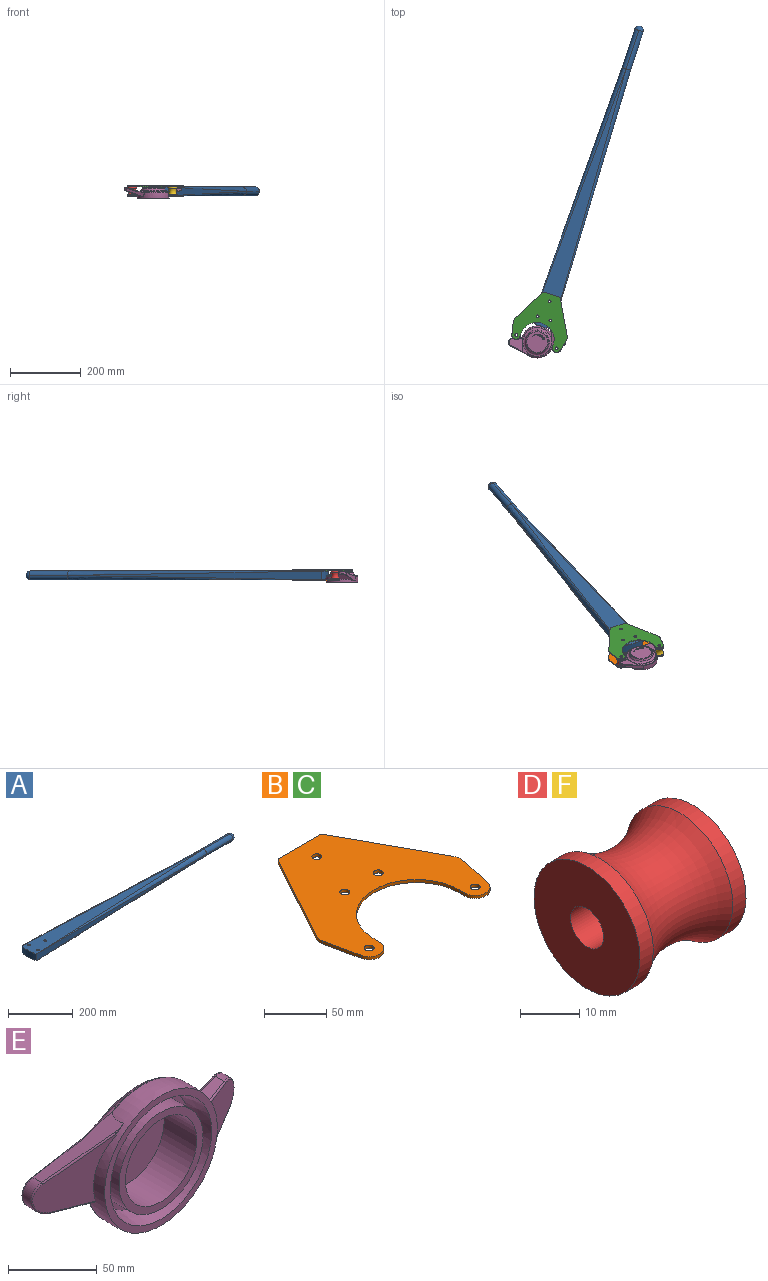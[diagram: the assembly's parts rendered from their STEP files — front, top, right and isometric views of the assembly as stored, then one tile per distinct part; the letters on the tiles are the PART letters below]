
ASSEMBLY  parts=6 mates=8
PART A: 25 faces, bbox 934.5x68.1x25.4 mm
  f0: plane 767.57x64.78mm, normal (0,0,1), area 23938.9mm2, adj f5,f8,f16,f22,f23,f24
  f1: cylinder r=101.76mm len=62.96mm, axis (0,0,-1), area 1577.1mm2, adj f6,f8,f13,f17
  f2: plane 763.77x24.64mm, normal (0.02,1,0), area 9383mm2, adj f5,f6,f11
  f3: sphere r=12.7mm, area 1013.4mm2, adj f4,f10,f15,f19
  f4: cylinder r=12.7mm len=114.46mm, axis (-1,0,0), area 2281.8mm2, adj f3,f5,f10,f15
  f5: bspline ~921.03x35.72mm, area 7832.2mm2, adj f0,f2,f4,f7
  f6: cylinder r=0.38mm len=24.64mm, axis (0,0,-1), area 12mm2, adj f1,f2,f7,f12
  f7: bspline ~0.38x0.38mm, area 0.1mm2, adj f5,f6,f8
  f8: torus R=101.38mm, axis (0,0,-1), area 38.3mm2, adj f0,f1,f7,f18
  f9: plane 767.57x64.78mm, normal (0,0,-1), area 23938.9mm2, adj f11,f13,f20,f22,f23,f24
  f10: cylinder r=12.7mm len=114.46mm, axis (-1,0,0), area 2281.8mm2, adj f3,f4,f11,f19
  f11: bspline ~921.03x35.72mm, area 7832.2mm2, adj f2,f9,f10,f12
  f12: bspline ~0.38x0.38mm, area 0.1mm2, adj f6,f11,f13
  f13: torus R=101.38mm, axis (0,0,1), area 38.3mm2, adj f1,f9,f12,f21
  f14: plane 763.77x24.64mm, normal (0.02,-1,0), area 9383mm2, adj f16,f17,f20
  f15: cylinder r=12.7mm len=114.46mm, axis (-1,0,0), area 2281.8mm2, adj f3,f4,f16,f19
  f16: bspline ~921.03x35.72mm, area 7832.2mm2, adj f0,f14,f15,f18
  f17: cylinder r=0.38mm len=24.64mm, axis (0,0,-1), area 12mm2, adj f1,f14,f18,f21
  f18: bspline ~0.38x0.38mm, area 0.1mm2, adj f8,f16,f17
  f19: cylinder r=12.7mm len=114.46mm, axis (-1,0,0), area 2281.8mm2, adj f3,f10,f15,f20
  f20: bspline ~921.03x35.72mm, area 7832.2mm2, adj f9,f14,f19,f21
  f21: bspline ~0.38x0.38mm, area 0.1mm2, adj f13,f17,f20
  f22: cylinder r=3.98mm len=25.4mm, axis (0,0,1), area 634.4mm2, adj f0,f9
  f23: cylinder r=3.98mm len=25.4mm, axis (0,0,1), area 634.4mm2, adj f0,f9
  f24: cylinder r=3.98mm len=25.4mm, axis (0,0,1), area 634.4mm2, adj f0,f9
PART B: 21 faces, bbox 159.6x151.6x3 mm
  f0: cylinder r=11.94mm len=23.62mm, axis (0,0,1), area 105.1mm2, adj f1,f13,f14,f15
  f1: plane 35.96x7.52mm, normal (-0.98,-0.2,0), area 110.2mm2, adj f0,f2,f14,f15
  f2: cylinder r=12.7mm len=8.69mm, axis (0,0,1), area 26.9mm2, adj f1,f3,f14,f15
  f3: plane 95.84x52.41mm, normal (-0.88,0.48,0), area 327.7mm2, adj f2,f4,f14,f15
  f4: cylinder r=3.17mm len=3mm, axis (0,0,1), area 10.2mm2, adj f3,f5,f14,f15
  f5: plane 46.09x3mm, normal (0,1,0), area 138.3mm2, adj f4,f6,f14,f15
  f6: cylinder r=3.17mm len=3mm, axis (0,0,1), area 10.2mm2, adj f5,f7,f14,f15
  f7: plane 95.84x52.41mm, normal (0.88,0.48,0), area 327.7mm2, adj f6,f8,f14,f15
  f8: cylinder r=12.7mm len=8.69mm, axis (0,0,1), area 26.9mm2, adj f7,f9,f14,f15
  f9: plane 35.96x7.52mm, normal (0.98,-0.2,0), area 110.2mm2, adj f8,f10,f14,f15
  f10: cylinder r=11.94mm len=23.62mm, axis (0,0,1), area 105.1mm2, adj f9,f11,f14,f15
  f11: plane 6.35x3mm, normal (-1,0,0), area 19mm2, adj f10,f12,f14,f15
  f12: cylinder r=48.39mm len=96.77mm, axis (0,0,1), area 456mm2, adj f11,f13,f14,f15
  f13: plane 6.35x3mm, normal (1,0,0), area 19mm2, adj f0,f12,f14,f15
  f14: plane 159.6x151.64mm, normal (0,0,-1), area 12441.6mm2, adj f0,f1,f2,f3,f4,f5,f6,f7
  f15: plane 159.6x151.64mm, normal (0,0,1), area 12441.6mm2, adj f0,f1,f2,f3,f4,f5,f6,f7
  f16: cylinder r=3.98mm len=7.95mm, axis (0,0,1), area 74.9mm2, adj f14,f15
  f17: cylinder r=3.98mm len=7.95mm, axis (0,0,1), area 74.9mm2, adj f14,f15
  f18: cylinder r=3.98mm len=7.95mm, axis (0,0,1), area 74.9mm2, adj f14,f15
  f19: cylinder r=3.98mm len=7.95mm, axis (0,0,1), area 74.9mm2, adj f14,f15
  f20: cylinder r=3.98mm len=7.95mm, axis (0,0,1), area 74.9mm2, adj f14,f15
PART C: same geometry as B
PART D: 6 faces, bbox 25.4x30.6x30.6 mm
  f0: plane 25.4x25.4mm, normal (1,0,0), area 457.1mm2, adj f1,f5
  f1: cylinder r=12.7mm len=25.4mm, axis (-1,0,0), area 253.4mm2, adj f0,f2
  f2: torus R=25.4mm, axis (-1,0,0), area 1360.5mm2, adj f1,f3
  f3: cylinder r=12.7mm len=25.4mm, axis (-1,0,0), area 253.4mm2, adj f2,f4
  f4: plane 25.4x25.4mm, normal (-1,0,0), area 457.1mm2, adj f3,f5
  f5: cylinder r=3.98mm len=25.4mm, axis (-1,0,0), area 634.4mm2, adj f0,f4
PART E: 111 faces, bbox 162.9x31.9x99.3 mm
  f0: plane 58.91x58.91mm, normal (0,1,0), area 2670.1mm2, adj f26,f55,f56,f57,f58,f64,f65,f66
  f1: plane 81.99x81.73mm, normal (0,1,0), area 374.9mm2, adj f2,f5,f11,f23,f24,f27,f30,f35
  f2: cylinder r=7mm len=38.39mm, axis (0,0,1), area 77.7mm2, adj f1,f3,f43,f47
  f3: plane 37.36x37.18mm, normal (0.29,0.96,0), area 1035.3mm2, adj f2,f44,f45,f46
  f4: plane 27.66x17.22mm, normal (0,0,-1), area 218mm2, adj f7,f10,f18,f25,f46,f47,f54
  f5: plane 5.19x4.14mm, normal (1,0,0), area 1.4mm2, adj f1,f17,f24,f42
  f6: plane 51.49x27.07mm, normal (-0.46,0,0.89), area 518.6mm2, adj f7,f8,f12,f18,f42,f43,f44,f52
  f7: cylinder r=12mm len=22.64mm, axis (0,-1,0), area 231.1mm2, adj f4,f6,f45,f53
  f8: plane 7.51x6.59mm, normal (0,-1,0), area 5.7mm2, adj f6,f9,f18,f52
  f9: plane 47.7x42.59mm, normal (-0.36,-0.93,0), area 1080.8mm2, adj f8,f18,f52,f53,f54
  f10: torus R=38.12mm, axis (0,1,0), area 327.7mm2, adj f4,f11,f25,f30,f35,f47
  f11: torus R=40.82mm, axis (0,1,0), area 113.7mm2, adj f1,f10,f30,f47,f48
  f12: torus R=42.54mm, axis (0,-1,0), area 70.5mm2, adj f6,f17,f18,f29,f42
  f13: plane 67.1x67.1mm, normal (0,-1,0), area 984.7mm2, adj f14,f22
  f14: cylinder r=28.5mm len=57mm, axis (0,1,0), area 4655.8mm2, adj f13,f15
  f15: plane 57x57mm, normal (0,-1,0), area 2551.8mm2, adj f14
  f16: cone r=31mm half-angle=26.6deg, axis (0,-1,0), area 1096.7mm2, adj f23,f26
  f17: torus R=38.12mm, axis (0,1,0), area 327.9mm2, adj f5,f12,f24,f29,f40,f42
  f18: revolved ~90.6x90.6mm, area 3305.4mm2, adj f4,f6,f8,f9,f12,f19,f25,f29
  f19: plane 90x90mm, normal (0,-1,0), area 1208.7mm2, adj f18,f20
  f20: cone r=40.5mm half-angle=11.3deg, axis (0,-1,0), area 3748.5mm2, adj f19,f21
  f21: plane 75x75mm, normal (0,-1,0), area 881.4mm2, adj f20,f22
  f22: cylinder r=33.55mm len=67.1mm, axis (0,1,0), area 3162.1mm2, adj f13,f21
  f23: torus R=40.33mm, axis (0,1,0), area 1793.5mm2, adj f1,f16
  f24: torus R=40.82mm, axis (0,1,0), area 114.3mm2, adj f1,f5,f17,f40,f41
  f25: torus R=42.54mm, axis (0,-1,0), area 70.5mm2, adj f4,f10,f18,f31,f35
  f26: torus R=29.45mm, axis (0,1,0), area 534mm2, adj f0,f16
  f27: cylinder r=7mm len=37.32mm, axis (0,0,-1), area 71.4mm2, adj f1,f28,f36,f40
  f28: plane 36.71x36.04mm, normal (-0.29,0.96,0), area 982.7mm2, adj f27,f37,f38,f39
  f29: plane 27.15x16.67mm, normal (0,0,1), area 203.7mm2, adj f12,f17,f18,f32,f39,f40,f51
  f30: plane 5.2x4.14mm, normal (-1,0,0), area 1.4mm2, adj f1,f10,f11,f35
  f31: plane 51.36x26.98mm, normal (0.46,0,-0.89), area 490.3mm2, adj f18,f25,f32,f33,f35,f36,f37,f49
  f32: cylinder r=12mm len=22.64mm, axis (0,-1,0), area 213.3mm2, adj f29,f31,f38,f50
  f33: plane 7.51x6.59mm, normal (0,-1,0), area 5.7mm2, adj f18,f31,f34,f49
  f34: plane 47.7x42.59mm, normal (0.36,-0.93,0), area 1080.8mm2, adj f18,f33,f49,f50,f51
  f35: bspline ~27.86x14.91mm, area 92.6mm2, adj f1,f10,f25,f30,f31,f36
  f36: bspline ~3.16x2.62mm, area 6.3mm2, adj f27,f31,f35,f37
  f37: cylinder r=1.5mm len=32.2mm, axis (-0.86,-0.26,-0.45), area 92.8mm2, adj f28,f31,f36,f38
  f38: bspline ~23.46x14.49mm, area 83.2mm2, adj f28,f32,f37,f39
  f39: cylinder r=1.5mm len=26.65mm, axis (0.96,0.29,0), area 64.5mm2, adj f28,f29,f38,f40
  f40: torus R=8.5mm, axis (0,0,1), area 3.8mm2, adj f17,f24,f27,f29,f39,f41
  f41: cylinder r=1.5mm len=0.63mm, axis (1,0,0), area 0.2mm2, adj f1,f24,f40
  f42: bspline ~27.58x14.32mm, area 82.6mm2, adj f1,f5,f6,f12,f17,f43
  f43: bspline ~2.78x2.1mm, area 4.1mm2, adj f2,f6,f42,f44
  f44: cylinder r=1mm len=32.2mm, axis (0.86,-0.26,0.45), area 62.6mm2, adj f3,f6,f43,f45
  f45: bspline ~23.4x14.35mm, area 56.2mm2, adj f3,f7,f44,f46
  f46: cylinder r=1mm len=26.65mm, axis (-0.96,0.29,0), area 43.3mm2, adj f3,f4,f45,f47
  f47: torus R=8mm, axis (0,0,-1), area 2.8mm2, adj f2,f4,f10,f11,f46,f48
  f48: cylinder r=1mm len=0.75mm, axis (-1,0,0), area 0.2mm2, adj f1,f11,f47
  f49: cylinder r=1mm len=44.4mm, axis (0.84,0.32,0.44), area 72mm2, adj f31,f33,f34,f50
  f50: bspline ~22.64x12mm, area 41.6mm2, adj f32,f34,f49,f51
  f51: cylinder r=1mm len=25.54mm, axis (-0.93,-0.36,0), area 42.3mm2, adj f18,f29,f34,f50
  f52: cylinder r=1mm len=44.4mm, axis (-0.84,0.32,-0.44), area 72mm2, adj f6,f8,f9,f53
  f53: bspline ~22.64x12mm, area 41.6mm2, adj f7,f9,f52,f54
  f54: cylinder r=1mm len=25.54mm, axis (0.93,-0.36,0), area 42.3mm2, adj f4,f9,f18,f53
  f55: extruded ~3.24x1.19mm, area 0.4mm2, adj f0,f56,f58,f59
  f56: extruded ~3.32x1.28mm, area 0.4mm2, adj f0,f55,f57,f59
  f57: extruded ~3.27x1.25mm, area 0.4mm2, adj f0,f56,f58,f59
  f58: extruded ~3.25x1.28mm, area 0.4mm2, adj f0,f55,f57,f59
  f59: plane 4.9x4.86mm, normal (0,1,0), area 8.1mm2, adj f55,f56,f57,f58,f60,f61,f62,f63
  f60: extruded ~2.53x0.92mm, area 0.3mm2, adj f59,f61,f63,f109
  f61: extruded ~2.41x1.02mm, area 0.3mm2, adj f59,f60,f62,f109
  f62: extruded ~2.47x0.9mm, area 0.3mm2, adj f59,f61,f63,f109
  f63: extruded ~2.38x0.96mm, area 0.3mm2, adj f59,f60,f62,f109
  f64: plane 0.56x0.3mm, normal (0.47,0,-0.89), area 0.1mm2, adj f0,f65,f73,f74
  f65: plane 4.1x2.15mm, normal (0.89,0,0.46), area 0.5mm2, adj f0,f64,f66,f74
  f66: plane 0.6x0.32mm, normal (-0.47,0,0.89), area 0.1mm2, adj f0,f65,f67,f74
  f67: plane 4.44x0.64mm, normal (-0.99,0,0.14), area 0.4mm2, adj f0,f66,f68,f74
  f68: plane 3.22x1.69mm, normal (0.89,0,0.46), area 0.4mm2, adj f0,f67,f69,f74
  f69: plane 0.56x0.3mm, normal (-0.47,0,0.89), area 0.1mm2, adj f0,f68,f70,f74
  f70: plane 4.1x2.15mm, normal (-0.89,0,-0.46), area 0.5mm2, adj f0,f69,f71,f74
  f71: plane 0.6x0.32mm, normal (0.47,0,-0.89), area 0.1mm2, adj f0,f70,f72,f74
  f72: plane 4.44x0.64mm, normal (0.99,0,-0.14), area 0.4mm2, adj f0,f71,f73,f74
  f73: plane 3.22x1.69mm, normal (-0.89,0,-0.46), area 0.4mm2, adj f0,f64,f72,f74
  f74: plane 5.93x5.65mm, normal (0,1,0), area 8.7mm2, adj f64,f65,f66,f67,f68,f69,f70,f71
  f75: plane 1.31x1.25mm, normal (0.69,0,-0.72), area 0.2mm2, adj f0,f76,f81,f82
  f76: plane 3.33x3.19mm, normal (0.72,0,0.69), area 0.5mm2, adj f0,f75,f77,f82
  f77: plane 1.25x1.2mm, normal (-0.69,0,0.72), area 0.2mm2, adj f0,f76,f78,f82
  f78: extruded ~0.67x0.6mm, area 0.1mm2, adj f0,f77,f79,f82
  f79: extruded ~0.75x0.3mm, area 0.1mm2, adj f0,f78,f80,f82
  f80: extruded ~1.91x0.75mm, area 0.2mm2, adj f0,f79,f81,f82
  f81: extruded ~3.3x0.85mm, area 0.4mm2, adj f0,f75,f80,f82
  f82: plane 5.37x5.36mm, normal (0,1,0), area 8.4mm2, adj f75,f76,f77,f78,f79,f80,f81,f83
  f83: plane 2.54x2.44mm, normal (-0.72,0,-0.69), area 0.4mm2, adj f82,f84,f89,f110
  f84: plane 0.76x0.73mm, normal (0.69,0,-0.72), area 0.1mm2, adj f82,f83,f85,f110
  f85: extruded ~0.66x0.56mm, area 0.1mm2, adj f82,f84,f86,f110
  f86: extruded ~1.79x0.61mm, area 0.2mm2, adj f82,f85,f87,f110
  f87: extruded ~1.38x0.72mm, area 0.2mm2, adj f82,f86,f88,f110
  f88: extruded ~1.11x0.62mm, area 0.1mm2, adj f82,f87,f89,f110
  f89: plane 0.77x0.74mm, normal (-0.69,0,0.72), area 0.1mm2, adj f82,f83,f88,f110
  f90: plane 2.61x0.53mm, normal (0.98,0,0.2), area 0.3mm2, adj f0,f91,f99,f100
  f91: plane 0.65x0.13mm, normal (-0.2,0,0.98), area 0.1mm2, adj f0,f90,f92,f100
  f92: plane 2.61x0.53mm, normal (-0.98,0,-0.2), area 0.3mm2, adj f0,f91,f93,f100
  f93: extruded ~2.32x1.66mm, area 0.3mm2, adj f0,f92,f94,f100
  f94: extruded ~2.38x1.62mm, area 0.3mm2, adj f0,f93,f95,f100
  f95: plane 2.61x0.53mm, normal (0.98,0,0.2), area 0.3mm2, adj f0,f94,f96,f100
  f96: plane 0.65x0.13mm, normal (-0.2,0,0.98), area 0.1mm2, adj f0,f95,f97,f100
  f97: plane 2.61x0.53mm, normal (-0.98,0,-0.2), area 0.3mm2, adj f0,f96,f98,f100
  f98: extruded ~1.7x1.02mm, area 0.2mm2, adj f0,f97,f99,f100
  f99: extruded ~1.62x1.24mm, area 0.2mm2, adj f0,f90,f98,f100
  f100: plane 5.06x4.48mm, normal (0,1,0), area 7mm2, adj f90,f91,f92,f93,f94,f95,f96,f97
  f101: plane 0.54x0.1mm, normal (-1,0,0), area 0.1mm2, adj f0,f102,f107,f108
  f102: cylinder r=20.88mm len=10.37mm, axis (0,1,0), area 1.1mm2, adj f0,f101,f103,f108
  f103: plane 0.25x0.1mm, normal (-1,0,0.01), area 0mm2, adj f0,f102,f104,f108
  f104: cylinder r=20.62mm len=10.24mm, axis (0,1,0), area 1.1mm2, adj f0,f103,f105,f108
  f105: plane 0.49x0.23mm, normal (-0.42,0,0.91), area 0.1mm2, adj f0,f104,f106,f108
  f106: plane 2.42x0.89mm, normal (-0.34,0,-0.94), area 0.3mm2, adj f0,f105,f107,f108
  f107: plane 1.86x1.79mm, normal (0.72,0,0.69), area 0.3mm2, adj f0,f101,f106,f108
  f108: plane 12.17x4.15mm, normal (0,1,0), area 4mm2, adj f101,f102,f103,f104,f105,f106,f107
  f109: plane 3.73x3.63mm, normal (0,1,0), area 10.4mm2, adj f60,f61,f62,f63
  f110: plane 3.9x3.88mm, normal (0,1,0), area 9mm2, adj f83,f84,f85,f86,f87,f88,f89
PART F: same geometry as D
PLACE A rot(axis=(0,0,1),71.8deg) t=(13.22,48.35,18.88)mm
PLACE B rot(axis=(-0.16,-0.99,0),180deg) t=(-2.45,0.83,3.18)mm
PLACE C rot(axis=(0,0,-1),18.2deg) t=(-2.45,0.83,34.58)mm
PLACE D rot(axis=(-0.22,-0.95,-0.22),92.8deg) t=(-59.74,19.72,18.88)mm
PLACE E rot(axis=(1,0,0),90deg) t=(0,0,0)mm fixed
PLACE F rot(axis=(-0.12,-0.98,-0.12),90.9deg) t=(54.84,-18.06,18.87)mm
MATE planar B.f14 <-> A.f9  axis (0,0,1) through (19.03,65.96,6.18)mm
MATE cylindrical B.f12 <-> C.f12  axis (0,0,-1) through (-0.46,6.86,4.68)mm
MATE fastened C.f16 <-> A.f24  axis (0,0,-1) through (1.09,72.41,31.58)mm
MATE planar B.f16 <-> E.f10  axis (0,0,-1) through (37.28,60.48,3.18)mm
MATE revolute D.f1 <-> C.f0  axis (0,0,-1) through (-59.74,19.72,31.58)mm
MATE planar C.f5 <-> B.f5  axis (0.31,0.95,0) through (41.29,133.5,33.08)mm
MATE planar A.f22 <-> C.f14  axis (0,0,1) through (35.09,114.69,31.58)mm
MATE revolute F.f1 <-> C.f10  axis (0,0,-1) through (54.84,-18.06,31.58)mm
